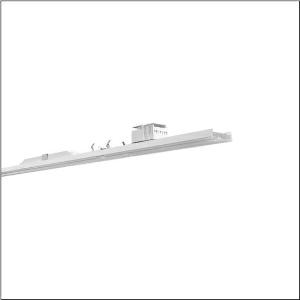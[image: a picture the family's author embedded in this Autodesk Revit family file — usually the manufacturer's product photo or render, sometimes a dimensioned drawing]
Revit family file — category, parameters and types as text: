
# Revit family: licross_r__21_recessed_mo_52tl12dne75f_abc3
name_source: partatom
category: Lighting Fixtures
units: mm (PartAtom-declared; Revit-internal decimal feet)

## family parameters
Cut with Voids When Loaded = No
Host = Face
Light Source = No
Part Type = Normal
Room Calculation Point = No
Round Connector Dimension = Use Diameter
Shared = No

## types (1)
- --- (1 x LED, 7970 lm, 61.1 W, 5000K)
    Apparent Load = 61 VA
    CIE Flux Codes = 72 92 99 100 100
    Color Rendering = 90
    Color Temperature = 5000K
    Default Elevation = 1800 mm
    Description = Licross® 21 Recessed MO, luminaire insert, of sheet steel, galvanised, coil coated, white, length: 1.500mm, width: 66mm, height: 67mm, LED rated luminous flux: 7.970lm, light colour: 950, control gear: DALI 2, control gear: ECG DALI, with plug, 5-pole, with phase selection, mains connection: 220..240V, AC, 50/60Hz, rated input power: 61W, halogen-free wiring, primary optical cover: cover, of PMMA, light emission: direct distribution, primary light characteristic: symmetric, protection rating (complete): IP40, insulation class (complete): insulation class I (protective earthing), certification: CE, ENEC, VDE, UKCA, protection symbol: D if used in an environment without relevant dust loads with corresponding accessories, impact resistance: IK06, permissible ambient temperature for indoor applications: -25..+35°C, corresponds to IFS (International Featured Standards) requirements for safety and quality in the food industry, reducing of maximum allowable ambient temperature of 5°C with ceiling mounting, LABS conformity tested according to VDMA 24364:2018-05, packaging unit: 1 piece
    Height = 58 mm
    Lamp = 1 x LED
    Lamp Light Flux = 7970 lm
    Lamp Power = 61.1 W
    Lamp count = 1
    Length = 1500 mm
    Luminous efficacy = 130 lm/W
    Manufacturer = Siteco
    ModVariant = No
    Model = 52TL12DNE75F
    Mounting Place = Ceiling
    Mounting Type = Pendant
    Number of Poles = 1
    OnlyDefault = Yes
    Power Factor = 1
    Product Name = Licross® 21 Recessed MO
    Product group = luminaire insert
    ProductGroupID = 901
    Protection Class = Protection class I
    Protection Degree = IP 40
    RLX_Detail_Level = 1
    RLX_Emergency_Light_Flux = 0 lm
    RLX_Emergency_Type = 0
    RLX_Emergency_Type_DB = No
    RlxData = <blob elided: 22601 chars, md5=357d695c>
    Socket = socket
    Standby Power = 0 W
    System Light Flux = 7970 lm
    System Power = 61 W
    Type Comments = factory setting: luminous flux: 100 % | dim-lin: 254 | 405 mA
    Type Image = l_1296935.jpg
    URL = http://relux.com
    VarID = @adj_135855
    Voltage = 0 V
    Weight = 0.00 kg
    Width = 66 mm

## geometry (parser evidence)
native form markers: Blend x4, Sweep x13
no freeform markers — native parametric forms only
